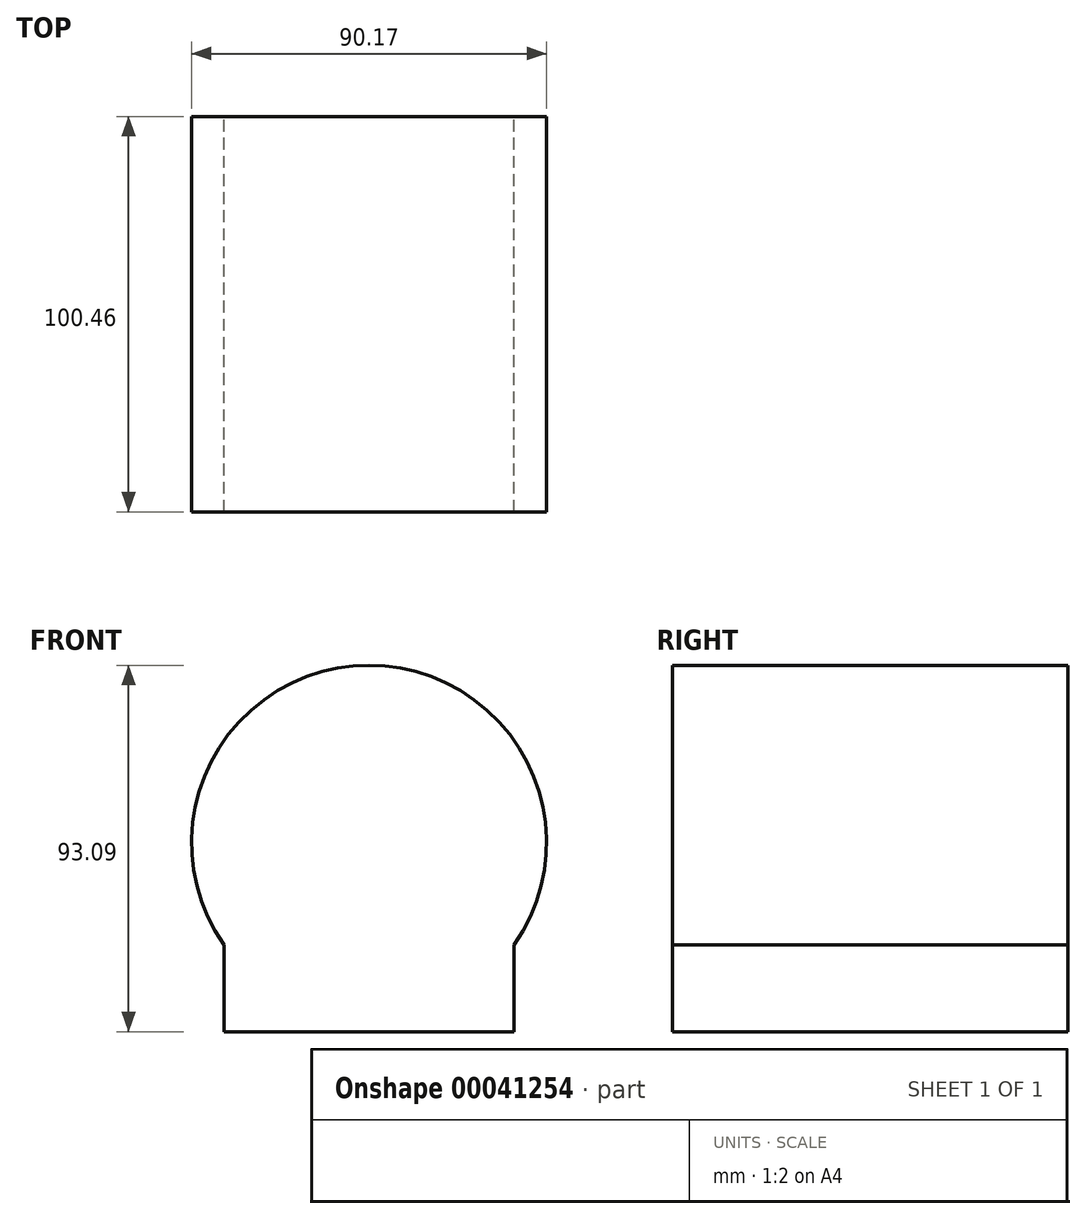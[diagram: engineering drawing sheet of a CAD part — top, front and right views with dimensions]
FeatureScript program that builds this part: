
annotation { "Feature Type Name" : "Feature", "Feature Type Description" : "" }
export const myFeature = defineFeature(function(context is Context, id is Id, definition is map)
    precondition{}
    {
        {
            var Q0;
            Q0=qCreatedBy(makeId("Front.planeOp"),FACE);
            var sketch = newSketch(context, id + "F0", { "sketchPlane" : qUnion([Q0])});
            skArc(sketch, "E0", {"start": v(36.83, -26) * mm, "mid": v(0, 45.08) * mm, "end": v(-36.83, -26) * mm});
            skLineSegment(sketch, "E1", {"start": v(-36.83, -48) * mm, "end": v(36.83, -48) * mm});
            skLineSegment(sketch, "E2", {"start": v(36.83, -48) * mm, "end": v(36.83, -26) * mm});
            skLineSegment(sketch, "E3", {"start": v(-36.83, -48) * mm, "end": v(-36.83, -26) * mm});
            skSolve(sketch);
        }
        {
            var Q0;
            Q0=makeQuery(id+"F0.imprint","IMPRINT",FACE,{"disambiguationData":[TD([[makeQuery(id+"F0.imprint","IMPRINT",EDGE,{"derivedFrom":sQuery(id+"F0.wireOp",EDGE,"E0")}),1.0]])]});
            extrude(context, id + "F1", {"entities" : qUnion([Q0]), "depth" : (3.96 * 25.4) * mm});
        }
    });
